# Revit family: POWER_PLUME
name_source: partatom
category: Mechanical Equipment
units: mm (PartAtom-declared; Revit-internal decimal feet)

## family parameters
Always vertical = Yes
Cut with Voids When Loaded = No
Part Type = Normal
Room Calculation Point = No
Round Connector Dimension = Use Radius
Shared = No
Work Plane-Based = No

## types (1)
- POWER_PLUME
    (T_SQ+.25")/2 = 2' - 7 1/8"
    0 = 0' - 0"
    1" = 0' - 1"
    1.5 = 0' - 1 1/2"
    10'-58 7/32" = 9' - 7 25/32"
    17.5" = 1' - 5 1/2"
    2" = 0' - 2"
    2' = 2' - 0"
    2.875" = 0' - 2 7/8"
    3" = 0' - 3"
    30.375" = 2' - 6 3/8"
    33 7/32"/2 = 1' - 4 5/8"
    39 27/32" = 3' - 3 27/32"
    4" = 0' - 4"
    44.375" = 3' - 8 3/8"
    44.375"/2 = 1' - 10 3/16"
    51" = 4' - 3"
    54.375" = 4' - 6 3/8"
    54.375"/2 = 2' - 3 3/16"
    58 7/32" = 4' - 10 7/32"
    64" = 5' - 4"
    8" = 0' - 8"
    A = 2' - 0 1/4"
    A/2 = 1' - 0 1/8"
    B = 2' - 0 1/8"
    B/2 = 1' - 0 1/16"
    C = 1' - 10 1/8"
    C/2 = 0' - 11 1/16"
    CONE_HEIGHT = 1' - 3 15/32"
    D = 1' - 9"
    E = 0' - 2"
    F = 0' - 0"
    Manufacturer = Loren Cook Company
    Model = Power Plume
    ONE EIGTH = 0' - 0 1/8"
    RAD = 2' - 1 7/8"
    RAD+1.5" = 2' - 3 3/8"
    RAD3 = 1' - 1"
    RAD_2 = 1' - 3"
    T_SQ = 5' - 2"
    T_SQ+.25" = 5' - 2 1/4"
    T_SQ/2 = 2' - 7"
    Type Comments = Power Plume with Curb Cap - Total of 10' Tall
    URL = www.lorencook.com

## geometry (parser evidence)
native form markers: Sweep x2
no freeform markers — native parametric forms only
